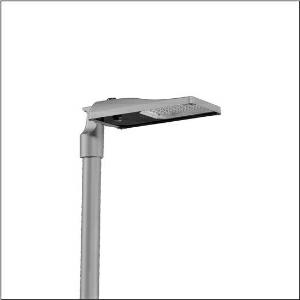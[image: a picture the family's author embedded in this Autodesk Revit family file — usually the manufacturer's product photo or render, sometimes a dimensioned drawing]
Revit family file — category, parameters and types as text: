
# Revit family: streetlight_sl_31_mini___st1_0a_5xh2d31t08ga_2aba
name_source: partatom
category: Lighting Fixtures
units: mm (PartAtom-declared; Revit-internal decimal feet)

## family parameters
Cut with Voids When Loaded = No
Host = Face
Light Source = No
Part Type = Normal
Room Calculation Point = No
Round Connector Dimension = Use Diameter
Shared = No

## types (1)
- --- (1 x LED, 5880 lm, 39.3 W, 3000K)
    Apparent Load = 39 VA
    CIE Flux Codes = 37 72 97 100 100
    Color Rendering = 70
    Color Temperature = 3000K
    Default Elevation = 1800 mm
    Description = Streetlight SL 31 mini D4i, Desk-Remote mast luminaire for post-top, side-entry; light control with lens of PMMA; light distribution: ST1.0a, direct asymmetric distribution, for standard-compliant lighting for roads and squares; LED: luminous flux: 5.880lm, light colour: 730, colour temperature: 3000K; luminous efficacy: 149,6lm/W; control: pre-setting: logarithmic dimming characteristic, flexible luminous flux parameterisation, time-dependent luminous flux control, constant luminous flux control, power reduction, intelligent temperature release in ECG and LED module, overheat protection; luminaire housing, of diecast aluminium, Siteco® metallic grey (DB 702S), corrosivity category C5 high according to DIN EN ISO 12944; cover of toughened safety glass, transparent, mast flange of diecast aluminium, Siteco® metallic grey (DB 702S), spigot size: 76/60mm, mast flange included unmounted; with cable H07RN-F 2x 1.5mm², cable length: 6,5m, connection cable pre-assembled; mains connection: 220..240V, AC, 50/60Hz; power consumption (at start of service life): 39,3W / (at end of service life): 40,7W / (with reduced operation 50%): 18,1W; protection rating (complete): IP66; insulation class (complete): insulation class II (safety insulation); impact resistance: IK09; certification: CE, ENEC, ENEC+, VDE, UKCA, ZD4i; permissible operating ambient temperature for outdoor applications: -40..+50°C; packaging unit: 1 piece

Light Distribution: ST1.0a
    Height = 76 mm
    Lamp = 1 x LED
    Lamp Light Flux = 5880 lm
    Lamp Power = 39.3 W
    Lamp count = 1
    Length = 547 mm
    Luminous efficacy = 150 lm/W
    Manufacturer = Siteco
    ModVariant = No
    Model = 5XH2D31T08GA
    Number of Poles = 1
    OnlyDefault = Yes
    Power Factor = 1
    Product Name = Streetlight SL 31 mini | ST1.0a
    Product group = mast luminaire | pylon top
    ProductGroupID = 6100
    Protection Class = Protection class II
    Protection Degree = IP 66
    RLX_Detail_Level = 1
    RLX_Emergency_Light_Flux = 0 lm
    RLX_Emergency_Type = 0
    RLX_Emergency_Type_DB = No
    RlxData = <blob elided: 39733 chars, md5=6057a574>
    Socket = socket
    Standby Power = 0 W
    System Light Flux = 5880 lm
    System Power = 39 W
    Type Comments = factory setting: luminous flux: 100 % | dim-lin: 254 | 798 mA
    Type Image = l_1300332.jpg
    URL = http://relux.com
    VarID = @adj_054744
    Voltage = 0 V
    Weight = 0.00 kg
    Width = 265 mm

## geometry (parser evidence)
native form markers: Blend x4, Sweep x9
no freeform markers — native parametric forms only
